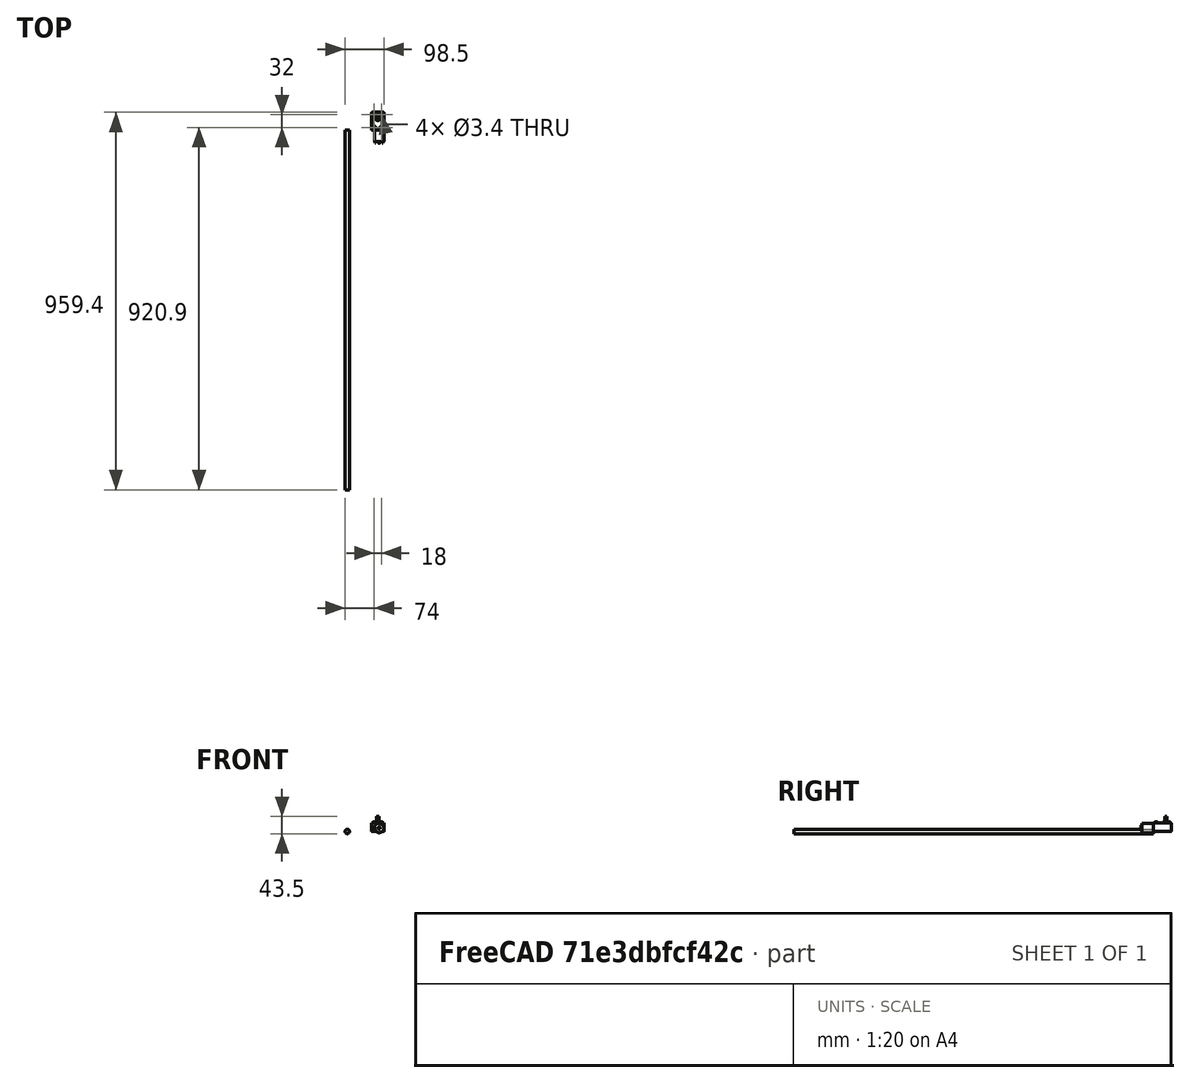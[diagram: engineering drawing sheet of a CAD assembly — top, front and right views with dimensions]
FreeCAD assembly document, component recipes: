
FREECAD ASSEMBLY — COMPONENT RECIPES ("chainsword_master")

This assembly document has 4 components, labeled P0..P3 below (a component is one placed body or linked part). 4 of them carry a construction recipe — the FreeCAD feature program that regenerates the part from scratch, quoted from this document or its linked companion documents; the rest are supplied as boundary geometry only. No exploded tour is included for this assembly.
COMPONENT P0 — recipe-attached ("Body", modeled in this document).
Construction recipe (the document's own serialized feature program — sketch geometry with constraints, then the solid features built on it; lengths are millimeters unless a unit is written):

FEATURE [Sketcher::SketchObject] Sketch
  ArcFitTolerance = 1e-06
  AttachmentSupport = -> [Origin002]
  ExternalTypes = [0]
  FullyConstrained = true
  MakeInternals = false
  MapMode = 5
  Placement = pos=(0,0,0) rot=(1,0,0;1.5708rad)
  _ExternalGeoVersion = 1
  sketch-geometry (1):
    g0: Circle CenterX=0 CenterY=0 CenterZ=0 NormalX=0 NormalY=0 NormalZ=1 AngleXU=0 Radius=5.5
  constraints (2):
    c: Diameter(g0) = 11
    c: Coincident(g0,g-1)
FEATURE [PartDesign::Pad] Pad
  Direction = (0,-1,2e-16)
  Length = 914.4
  Length2 = 10
  Profile = -> Sketch
  ReferenceAxis = -> Sketch [N_Axis]
  Refine = true
  SideType = 0
  Suppressed = false
  Type = 0
  Type2 = 0
FEATURE [PartDesign::Body] Body  label="threaded_rod"
  AllowCompound = false
  Group = -> [Sketch,Pad]
  Origin = -> Origin002
  Placement = pos=(133,0,0) rot=(0,0,1;0rad)
  Tip = -> Pad
COMPONENT P1 — recipe-attached ("housing", modeled in this document).
Construction recipe (the document's own serialized feature program — sketch geometry with constraints, then the solid features built on it; lengths are millimeters unless a unit is written):

FEATURE [Sketcher::SketchObject] Sketch001
  ArcFitTolerance = 1e-06
  AttachmentSupport = -> [Origin004]
  ExternalTypes = [0]
  FullyConstrained = true
  MakeInternals = false
  MapMode = 5
  _ExternalGeoVersion = 1
  sketch-geometry (4):
    g0: LineSegment StartX=0 StartY=0 StartZ=0 EndX=31 EndY=0 EndZ=0
    g1: LineSegment StartX=31 StartY=0 StartZ=0 EndX=31 EndY=45 EndZ=0
    g2: LineSegment StartX=31 StartY=45 StartZ=0 EndX=0 EndY=45 EndZ=0
    g3: LineSegment StartX=0 StartY=45 StartZ=0 EndX=0 EndY=0 EndZ=0
  constraints (11):
    c: Coincident(g0,g1)
    c: Coincident(g1,g2)
    c: Coincident(g2,g3)
    c: Coincident(g3,g0)
    c: Horizontal(g0)
    c: Horizontal(g2)
    c: Vertical(g1)
    c: Vertical(g3)
    c: Distance(g1,g3) = 31
    c: Distance(g0,g2) = 45
    c: Coincident(g0,g-1)
FEATURE [PartDesign::Pad] Pad001
  Direction = (0,0,1)
  Length = 22
  Length2 = 10
  Profile = -> Sketch001
  ReferenceAxis = -> Sketch001 [N_Axis]
  Refine = true
  SideType = 0
  Suppressed = false
  Type = 0
  Type2 = 0
FEATURE [Sketcher::SketchObject] Sketch002
  ArcFitTolerance = 1e-06
  AttachmentSupport = -> [Pad001]
  ExternalGeometry = -> [Pad001]
  ExternalTypes = [0]
  FullyConstrained = true
  MakeInternals = false
  MapMode = 5
  Placement = pos=(0,0,0) rot=(1,0,0;1.5708rad)
  _ExternalGeoVersion = 1
  sketch-geometry (1):
    g0: Circle CenterX=19 CenterY=9 CenterZ=0 NormalX=0 NormalY=0 NormalZ=1 AngleXU=0 Radius=12
  constraints (3):
    c: Diameter(g0) = 24
    c: Distance(g0,g-1) = 3
    c: Tangent(g0,g-3)
FEATURE [PartDesign::Pad] Pad002
  BaseFeature = -> Pad001
  Direction = (0,-1,2e-16)
  Length = 30
  Length2 = 10
  Profile = -> Sketch002 [Edge1]
  ReferenceAxis = -> Sketch002 [N_Axis]
  Refine = true
  SideType = 0
  Suppressed = false
  Type = 0
  Type2 = 0
FEATURE [Sketcher::SketchObject] Sketch003
  ArcFitTolerance = 1e-06
  AttachmentSupport = -> [Pad002]
  ExternalGeometry = -> [Pad002]
  ExternalTypes = [0]
  FullyConstrained = false
  MakeInternals = false
  MapMode = 5
  Placement = pos=(0,-30,0) rot=(1,0,0;1.5708rad)
  _ExternalGeoVersion = 1
  sketch-geometry (9):
    g0: LineSegment StartX=26.7462 StartY=15.1042 StartZ=0 EndX=28.7462 EndY=15.1042 EndZ=0
    g1: LineSegment StartX=28.7462 StartY=15.1042 StartZ=0 EndX=28.7462 EndY=14.9042 EndZ=0
    g2: LineSegment StartX=28.7462 StartY=14.9042 StartZ=0 EndX=26.7462 EndY=14.9042 EndZ=0
    g3: LineSegment StartX=26.7462 StartY=14.9042 StartZ=0 EndX=26.7462 EndY=15.1042 EndZ=0
    g4: LineSegment StartX=8.30695 StartY=4.56812 StartZ=0 EndX=10.307 EndY=4.56812 EndZ=0
    g5: LineSegment StartX=10.307 StartY=4.56812 StartZ=0 EndX=10.307 EndY=4.76812 EndZ=0
    g6: LineSegment StartX=10.307 StartY=4.76812 StartZ=0 EndX=8.30695 EndY=4.76812 EndZ=0
    g7: LineSegment StartX=8.30695 StartY=4.76812 StartZ=0 EndX=8.30695 EndY=4.56812 EndZ=0
    g8: Circle CenterX=19 CenterY=9 CenterZ=0 NormalX=0 NormalY=0 NormalZ=1 AngleXU=0 Radius=2.5
  constraints (24):
    c: Coincident(g0,g1)
    c: Coincident(g1,g2)
    c: Coincident(g2,g3)
    c: Coincident(g3,g0)
    c: Horizontal(g0)
    c: Horizontal(g2)
    c: Vertical(g1)
    c: Vertical(g3)
    c: Coincident(g4,g5)
    c: Coincident(g5,g6)
    c: Coincident(g6,g7)
    c: Coincident(g7,g4)
    c: Horizontal(g4)
    c: Horizontal(g6)
    c: Vertical(g5)
    c: Vertical(g7)
    c: Distance(g5,g7) = 2
    c: Distance(g4,g6) = 0.2
    c: Equal(g2,g6)
    c: Equal(g7,g3)
    c: Distance(g6,g-3) = 0.5
    c: Distance(g0,g-3) = 0.5
    c: Coincident(g8,g-3)
    c: Diameter(g8) = 5
FEATURE [PartDesign::Pad] Pad003
  BaseFeature = -> Pad002
  Direction = (0,-1,2e-16)
  Length = 3
  Length2 = 10
  Profile = -> Sketch003
  ReferenceAxis = -> Sketch003 [N_Axis]
  Refine = true
  SideType = 0
  Suppressed = false
  Type = 0
  Type2 = 0
FEATURE [PartDesign::Fillet] Fillet
  Base = -> Pad003 [Edge39]
  BaseFeature = -> Pad003
  Radius = 0.1
  Refine = true
  SupportTransform = false
  Suppressed = false
  UseAllEdges = false
FEATURE [PartDesign::Fillet] Fillet001
  Base = -> Fillet [Edge42,Edge43,Edge44,Edge40,Edge35,Edge38,Edge49,Edge45]
  BaseFeature = -> Fillet
  Radius = 1
  Refine = true
  SupportTransform = false
  Suppressed = false
  UseAllEdges = false
FEATURE [Sketcher::SketchObject] Sketch004
  ArcFitTolerance = 1e-06
  AttachmentSupport = -> [Fillet001]
  ExternalGeometry = -> [Fillet001]
  ExternalTypes = [0,0]
  FullyConstrained = true
  MakeInternals = false
  MapMode = 5
  Placement = pos=(0,0,22) rot=(0,0,1;0rad)
  _ExternalGeoVersion = 1
  sketch-geometry (5):
    g0: Circle CenterX=6.5 CenterY=6.5 CenterZ=0 NormalX=0 NormalY=0 NormalZ=1 AngleXU=0 Radius=3.5
    g1: Circle CenterX=6.5 CenterY=38.5 CenterZ=0 NormalX=0 NormalY=0 NormalZ=1 AngleXU=0 Radius=3.5
    g2: Circle CenterX=24.5 CenterY=6.5 CenterZ=0 NormalX=0 NormalY=0 NormalZ=1 AngleXU=0 Radius=3.5
    g3: Circle CenterX=24.5 CenterY=38.5 CenterZ=0 NormalX=0 NormalY=0 NormalZ=1 AngleXU=0 Radius=3.5
    g4: Circle CenterX=15.5 CenterY=30.5 CenterZ=0 NormalX=0 NormalY=0 NormalZ=1 AngleXU=0 Radius=6.5
  constraints (15):
    c: Diameter(g0) = 7
    c: Distance(g0,g-2) = 3
    c: Distance(g0,g-1) = 3
    c: Equal(g0,g1)
    c: Equal(g0,g2)
    c: Equal(g0,g3)
    c: Distance(g1,g-3) = 3
    c: Distance(g1,g-2) = 3
    c: Distance(g3,g-3) = 3
    c: Distance(g3,g-4) = 3
    c: Distance(g2,g-4) = 3
    c: Distance(g2,g-1) = 3
    c: Diameter(g4) = 13
    c: Distance(g4,g-3) = 8
    c: Distance(g4,g-2) = 9
FEATURE [PartDesign::Pad] Pad004
  BaseFeature = -> Fillet001
  Direction = (0,0,1)
  Length = 2
  Length2 = 10
  Profile = -> Sketch004
  ReferenceAxis = -> Sketch004 [N_Axis]
  Refine = true
  SideType = 0
  Suppressed = false
  Type = 0
  Type2 = 0
FEATURE [PartDesign::Hole] Hole
  BaseFeature = -> Pad004
  BaseProfileType = 7
  CustomThreadClearance = 0
  Depth = 3
  DepthType = 0
  Diameter = 3.4
  DrillForDepth = false
  DrillPoint = 1
  DrillPointAngle = 118
  HoleCutCountersinkAngle = 90
  HoleCutCustomValues = false
  HoleCutDepth = 0
  HoleCutDiameter = 0
  HoleCutType = 0
  ModelThread = false
  Profile = -> Pad004 [Face43,Face41,Face39,Face40]
  Refine = true
  Suppressed = false
  Tapered = false
  TaperedAngle = 90
  ThreadClass = 0
  ThreadDepth = 3
  ThreadDepthType = 0
  ThreadDiameter = 3
  ThreadDirection = 0
  ThreadFit = 0
  ThreadSize = 9
  ThreadType = 1
  Threaded = false
  UseCustomThreadClearance = false
FEATURE [PartDesign::Fillet] Fillet002
  Base = -> Hole [Edge80,Edge84,Edge88,Edge82,Edge86]
  BaseFeature = -> Hole
  Radius = 0.2
  Refine = true
  SupportTransform = false
  Suppressed = false
  UseAllEdges = false
FEATURE [Sketcher::SketchObject] Sketch005
  ArcFitTolerance = 1e-06
  AttachmentSupport = -> [Fillet002]
  ExternalGeometry = -> [Fillet002]
  ExternalTypes = [0]
  FullyConstrained = true
  MakeInternals = false
  MapMode = 5
  Placement = pos=(0,0,24) rot=(0,0,1;0rad)
  _ExternalGeoVersion = 1
  sketch-geometry (1):
    g0: Circle CenterX=15.5 CenterY=30.5 CenterZ=0 NormalX=0 NormalY=0 NormalZ=1 AngleXU=0 Radius=3
  constraints (2):
    c: Diameter(g0) = 6
    c: Coincident(g0,g-3)
FEATURE [PartDesign::Pad] Pad005
  BaseFeature = -> Fillet002
  Direction = (0,0,1)
  Length = 14
  Length2 = 10
  Profile = -> Sketch005
  ReferenceAxis = -> Sketch005 [N_Axis]
  Refine = true
  SideType = 0
  Suppressed = false
  Type = 0
  Type2 = 0
FEATURE [Sketcher::SketchObject] Sketch006
  ArcFitTolerance = 1e-06
  AttachmentSupport = -> [Pad005]
  ExternalGeometry = -> [Pad005]
  ExternalTypes = [0]
  FullyConstrained = false
  MakeInternals = false
  MapMode = 5
  Placement = pos=(0,0,38) rot=(0,0,1;0rad)
  _ExternalGeoVersion = 1
  sketch-geometry (4):
    g0: LineSegment StartX=14.0077 StartY=27.8975 StartZ=0 EndX=14.0077 EndY=27.0465 EndZ=0
    g1: LineSegment StartX=14.0077 StartY=27.0465 StartZ=0 EndX=17.0077 EndY=27.0465 EndZ=0
    g2: LineSegment StartX=17.0077 StartY=27.0465 StartZ=0 EndX=17.0077 EndY=27.8975 EndZ=0
    g3: LineSegment StartX=17.0077 StartY=27.8975 StartZ=0 EndX=14.0077 EndY=27.8975 EndZ=0
  constraints (10):
    c: Coincident(g0,g1)
    c: Coincident(g1,g2)
    c: Coincident(g2,g3)
    c: Coincident(g3,g0)
    c: Vertical(g0)
    c: Vertical(g2)
    c: Horizontal(g1)
    c: Horizontal(g3)
    c: PointOnObject(g0,g-3)
    c: DistanceX(g3,g3) = 3
FEATURE [PartDesign::Pocket] Pocket
  BaseFeature = -> Pad005
  Direction = (0,0,-1)
  Length = 12
  Length2 = 5
  Profile = -> Sketch006
  ReferenceAxis = -> Sketch006 [N_Axis]
  Refine = true
  SideType = 0
  Suppressed = false
  Type = 0
  Type2 = 0
FEATURE [PartDesign::Body] Body001  label="12v_DC_Motor"
  AllowCompound = true
  Group = -> [Sketch001,Pad001,Sketch002,Pad002,Sketch003,Pad003,Fillet,Fillet001,Sketch004,Pad004,Hole,Fillet002,Sketch005,Pad005,Sketch006,Pocket]
  Origin = -> Origin004
  Placement = pos=(195,0,0) rot=(0,0,1;0rad)
  Tip = -> Pocket
COMPONENT P2 — same part as P1; its construction recipe is shown at P1.
COMPONENT P3 — same part as P0; its construction recipe is shown at P0.
PROVENANCE & LICENSES
A FreeCAD (.FCStd) document from a public repository crawl; recipes are the document's own serialized feature recipes (and, for linked parts, companion documents' recipes).
License: as declared in the source repository (recorded in the dataset sidecar).
